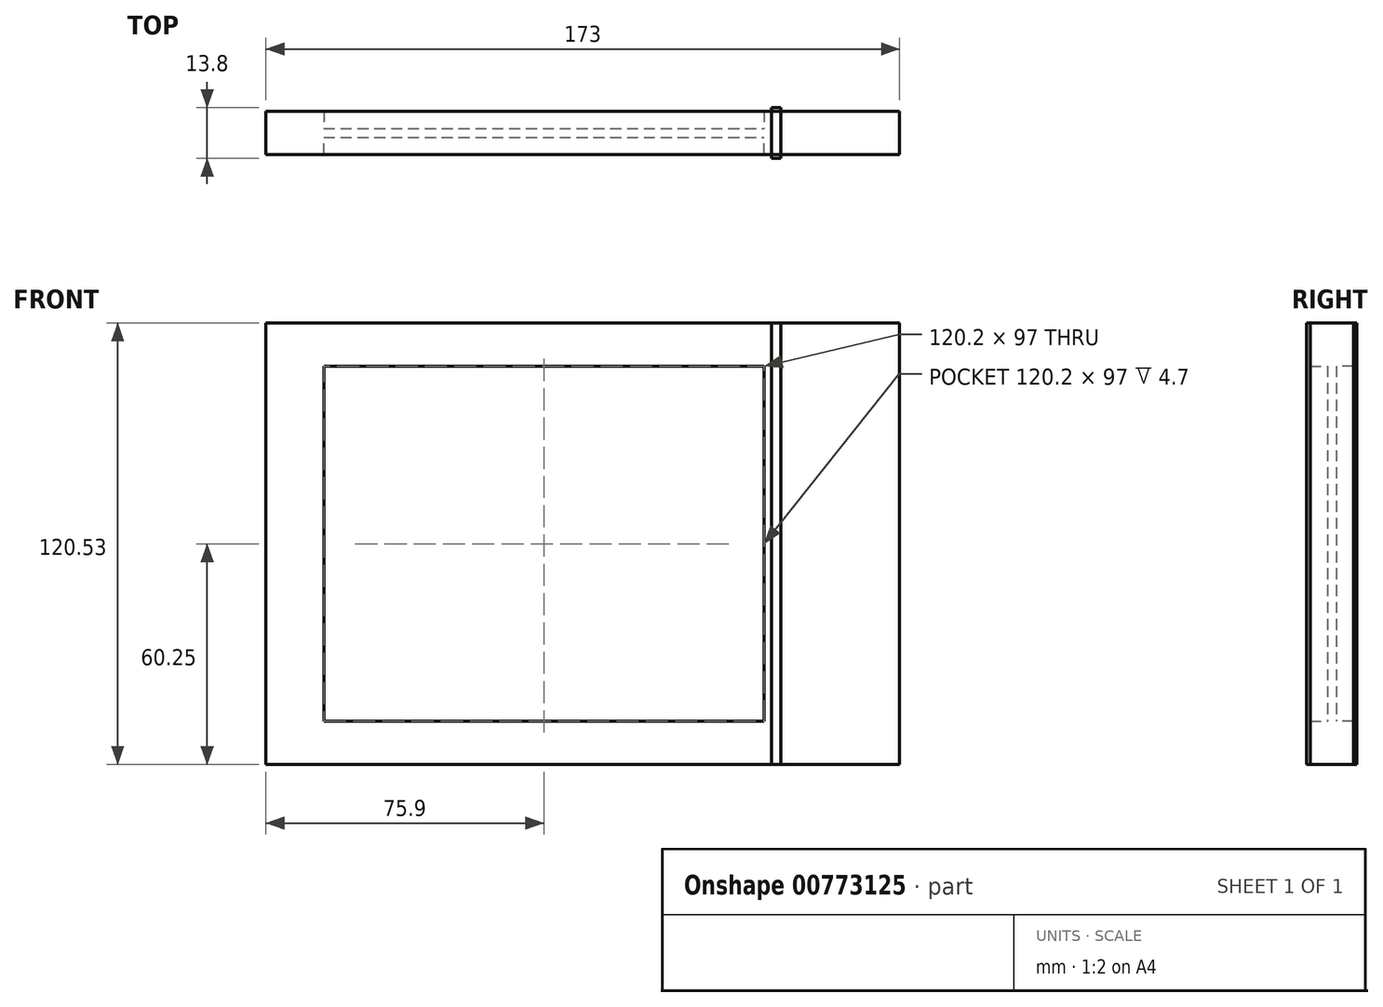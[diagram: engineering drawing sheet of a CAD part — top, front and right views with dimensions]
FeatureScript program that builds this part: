
annotation { "Feature Type Name" : "Feature", "Feature Type Description" : "" }
export const myFeature = defineFeature(function(context is Context, id is Id, definition is map)
    precondition{}
    {
        {
            var Q0;
            Q0=qCreatedBy(makeId("Front.planeOp"),FACE);
            var sketch = newSketch(context, id + "F0", { "sketchPlane" : qUnion([Q0])});
            skLineSegment(sketch, "E0.bottom", {"start": v(-86.5, 60.25) * mm, "end": v(86.5, 60.25) * mm});
            skLineSegment(sketch, "E0.top", {"start": v(-86.5, -60.25) * mm, "end": v(86.5, -60.25) * mm});
            skLineSegment(sketch, "E0.left", {"start": v(-86.5, 60.25) * mm, "end": v(-86.5, -60.25) * mm});
            skLineSegment(sketch, "E0.right", {"start": v(86.5, 60.25) * mm, "end": v(86.5, -60.25) * mm});
            skLineSegment(sketch, "E1.bottom", {"start": v(-70.7, 48.5) * mm, "end": v(49.5, 48.5) * mm});
            skLineSegment(sketch, "E1.top", {"start": v(-70.7, -48.5) * mm, "end": v(49.5, -48.5) * mm});
            skLineSegment(sketch, "E1.left", {"start": v(-70.7, 48.5) * mm, "end": v(-70.7, -48.5) * mm});
            skLineSegment(sketch, "E1.right", {"start": v(49.5, 48.5) * mm, "end": v(49.5, -48.5) * mm});
            skLineSegment(sketch, "E2.bottom", {"start": v(51.5, 60.28) * mm, "end": v(54, 60.28) * mm});
            skLineSegment(sketch, "E2.top", {"start": v(51.5, -60.22) * mm, "end": v(54, -60.22) * mm});
            skLineSegment(sketch, "E2.left", {"start": v(51.5, 60.28) * mm, "end": v(51.5, -60.22) * mm});
            skLineSegment(sketch, "E2.right", {"start": v(54, 60.28) * mm, "end": v(54, -60.22) * mm});
            skSolve(sketch);
        }
        {
            var Q0;
            Q0=qSketchRegion(id+"F0",true);
            extrude(context, id + "F1", {"entities" : qUnion([Q0]), "depth" : 5.9 * mm, "offsetDistance" : 25 * mm});
        }
        {
            var Q0;
            {var subQ5=sQuery(id+"F0.wireOp",EDGE,"E2.top");Q0=makeQuery(id+"F0.imprint","IMPRINT",FACE,{"disambiguationData":[TD([[makeQuery(id+"F0.imprint","IMPRINT",EDGE,{"derivedFrom":subQ5}),1.0]])]});}
            extrude(context, id + "F2", {"entities" : qUnion([Q0]), "operationType" : NewBodyOperationType.ADD, "depth" : 6.9 * mm, "offsetDistance" : 25 * mm});
        }
        {
            var Q0;
            Q0=makeQuery(id+"F0.imprint","IMPRINT",FACE,{"disambiguationData":[TD([[makeQuery(id+"F0.imprint","IMPRINT",EDGE,{"derivedFrom":sQuery(id+"F0.wireOp",EDGE,"E1.bottom")}),-1.0]])]});
            extrude(context, id + "F3", {"entities" : qUnion([Q0]), "operationType" : NewBodyOperationType.ADD, "depth" : 1.2 * mm, "offsetDistance" : 25 * mm});
        }
        {
            var Q0;
            Q0=makeQuery(id+"F1.opExtrude","SWEPT_BODY",BODY,{"disambiguationData":[OSD([sQuery(id+"F0.wireOp",EDGE,"E0.bottom"),sQuery(id+"F0.wireOp",EDGE,"E0.top"),sQuery(id+"F0.wireOp",EDGE,"E0.left"),sQuery(id+"F0.wireOp",EDGE,"E0.right"),sQuery(id+"F0.wireOp",EDGE,"E1.bottom"),sQuery(id+"F0.wireOp",EDGE,"E1.top"),sQuery(id+"F0.wireOp",EDGE,"E1.left"),sQuery(id+"F0.wireOp",EDGE,"E1.right"),sQuery(id+"F0.wireOp",EDGE,"E2.top"),sQuery(id+"F0.wireOp",EDGE,"E2.left"),sQuery(id+"F0.wireOp",EDGE,"E2.right")])]});
            var Q1;
            Q1=makeQuery(id+"F1.opExtrude","CAP_FACE",FACE,{"disambiguationData":[OSD([sQuery(id+"F0.wireOp",EDGE,"E0.bottom"),sQuery(id+"F0.wireOp",EDGE,"E0.top"),sQuery(id+"F0.wireOp",EDGE,"E0.left"),sQuery(id+"F0.wireOp",EDGE,"E0.right"),sQuery(id+"F0.wireOp",EDGE,"E1.bottom"),sQuery(id+"F0.wireOp",EDGE,"E1.top"),sQuery(id+"F0.wireOp",EDGE,"E1.left"),sQuery(id+"F0.wireOp",EDGE,"E1.right"),sQuery(id+"F0.wireOp",EDGE,"E2.bottom"),sQuery(id+"F0.wireOp",EDGE,"E2.left"),sQuery(id+"F0.wireOp",EDGE,"E2.right")])],"isStart":true});
            mirror(context, id + "F4", {"operationType" : NewBodyOperationType.ADD, "entities" : qUnion([Q0]), "mirrorPlane" : qUnion([Q1])});
        }
    });
